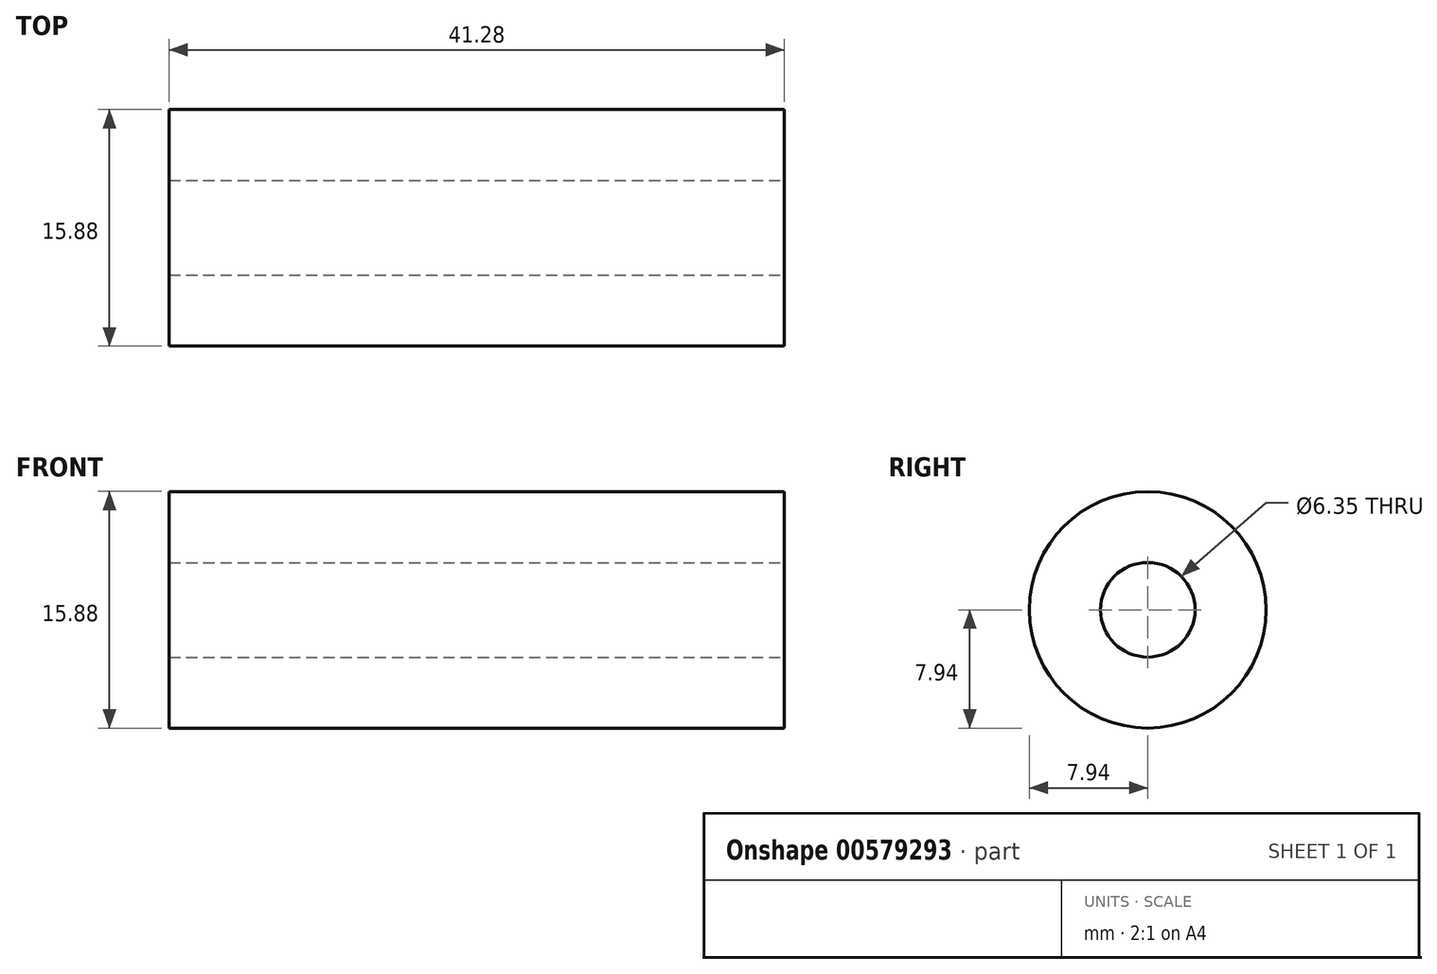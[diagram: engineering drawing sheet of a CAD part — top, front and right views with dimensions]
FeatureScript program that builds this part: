
annotation { "Feature Type Name" : "Feature", "Feature Type Description" : "" }
export const myFeature = defineFeature(function(context is Context, id is Id, definition is map)
    precondition{}
    {
        {
            var Q0;
            Q0=qCreatedBy(makeId("Right.planeOp"),FACE);
            var sketch = newSketch(context, id + "F0", { "sketchPlane" : qUnion([Q0])});
            skCircle(sketch, "E0", {"center": v(0, 0) * mm, "radius": 7.94 * mm});
            skSolve(sketch);
        }
        {
            var Q0;
            Q0=makeQuery(id+"F0.imprint","IMPRINT",FACE,{"disambiguationData":[TD([[makeQuery(id+"F0.imprint","IMPRINT",EDGE,{"derivedFrom":sQuery(id+"F0.wireOp",EDGE,"E0")}),1.0]])]});
            extrude(context, id + "F1", {"entities" : qUnion([Q0]), "depth" : 41.27 * mm, "offsetDistance" : 25.4 * mm});
        }
        {
            var Q0;
            Q0=makeQuery(id+"F1.opExtrude","CAP_FACE",FACE,{"disambiguationData":[OSD([sQuery(id+"F0.wireOp",EDGE,"E0")])],"isStart":false});
            var sketch = newSketch(context, id + "F2", { "sketchPlane" : qUnion([Q0])});
            skCircle(sketch, "E1", {"center": v(0, 0) * mm, "radius": 3.18 * mm});
            skSolve(sketch);
        }
        {
            var Q0;
            Q0=makeQuery(id+"F2.imprint","IMPRINT",FACE,{"disambiguationData":[TD([[makeQuery(id+"F2.imprint","IMPRINT",EDGE,{"derivedFrom":sQuery(id+"F2.wireOp",EDGE,"E1")}),1.0]])]});
            extrude(context, id + "F3", {"entities" : qUnion([Q0]), "operationType" : NewBodyOperationType.REMOVE, "oppositeDirection" : true, "depth" : 41.27 * mm, "offsetDistance" : 25.4 * mm});
        }
    });
